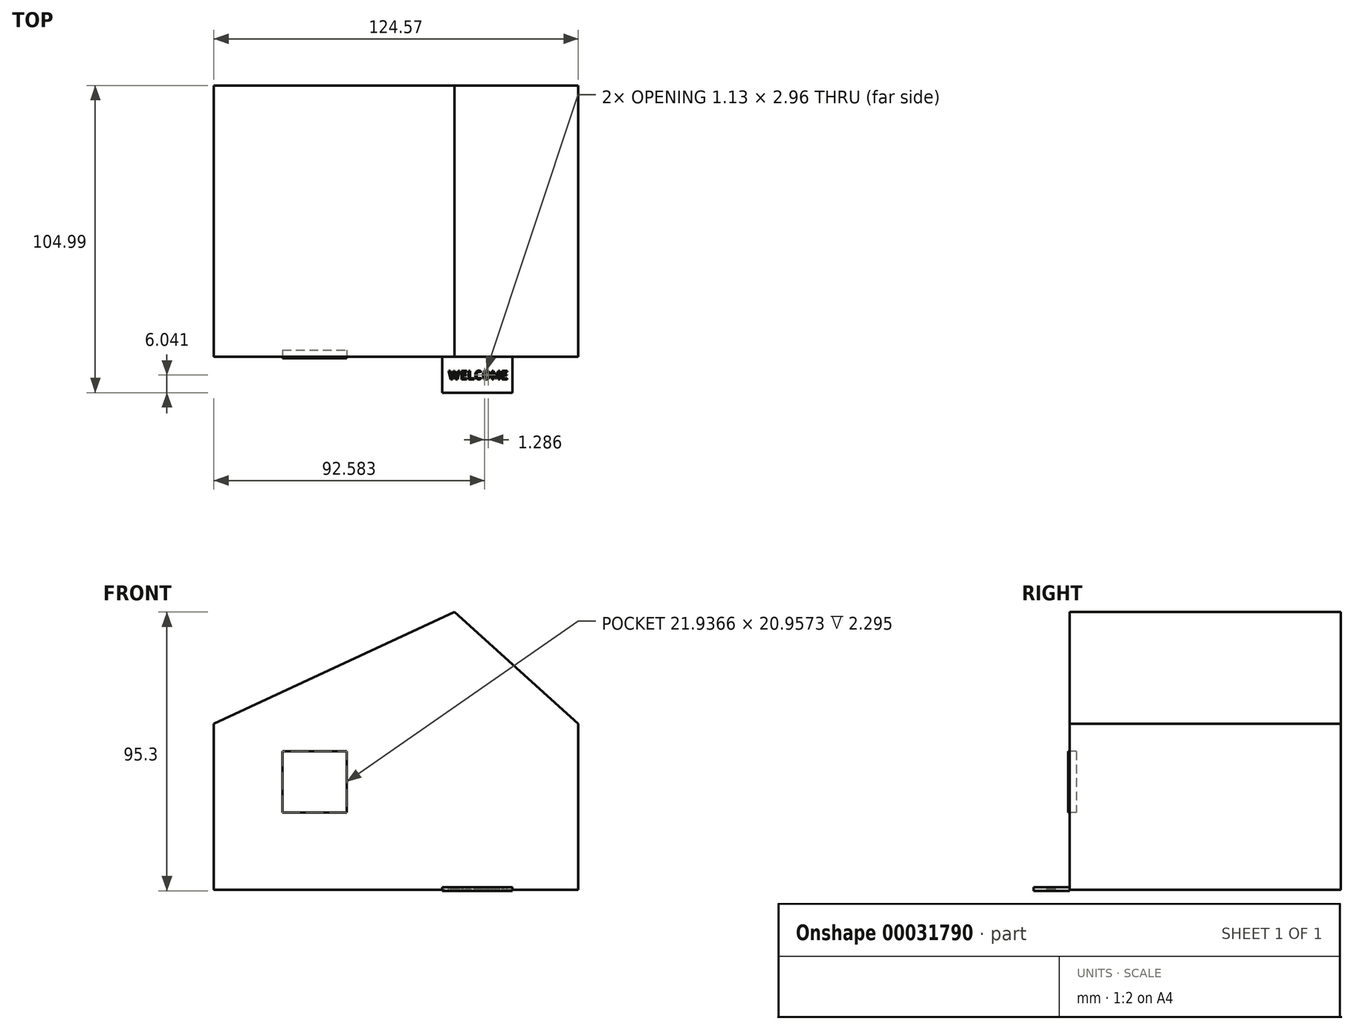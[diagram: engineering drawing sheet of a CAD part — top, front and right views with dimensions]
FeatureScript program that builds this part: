
annotation { "Feature Type Name" : "Feature", "Feature Type Description" : "" }
export const myFeature = defineFeature(function(context is Context, id is Id, definition is map)
    precondition{}
    {
        {
            var Q0;
            Q0=qCreatedBy(makeId("Front.planeOp"),FACE);
            var sketch = newSketch(context, id + "F0", { "sketchPlane" : qUnion([Q0])});
            skLineSegment(sketch, "E0.bottom", {"start": v(-56.21, 22.82) * mm, "end": v(68.36, 22.82) * mm});
            skLineSegment(sketch, "E0.top", {"start": v(-56.21, -33.98) * mm, "end": v(68.36, -33.98) * mm});
            skLineSegment(sketch, "E0.left", {"start": v(-56.21, 22.82) * mm, "end": v(-56.21, -33.98) * mm});
            skLineSegment(sketch, "E0.right", {"start": v(68.36, 22.82) * mm, "end": v(68.36, -33.98) * mm});
            skLineSegment(sketch, "E1", {"start": v(-56.21, 22.82) * mm, "end": v(26.05, 61.01) * mm});
            skLineSegment(sketch, "E2", {"start": v(26.05, 61.01) * mm, "end": v(68.36, 22.82) * mm});
            skSolve(sketch);
        }
        {
            var Q0;
            Q0=makeQuery(id+"F0.imprint","IMPRINT",FACE,{"disambiguationData":[TD([[makeQuery(id+"F0.imprint","IMPRINT",EDGE,{"derivedFrom":sQuery(id+"F0.wireOp",EDGE,"E0.bottom")}),1.0]])]});
            var Q1;
            Q1=makeQuery(id+"F0.imprint","IMPRINT",FACE,{"disambiguationData":[TD([[makeQuery(id+"F0.imprint","IMPRINT",EDGE,{"derivedFrom":sQuery(id+"F0.wireOp",EDGE,"E0.bottom")}),-1.0]])]});
            extrude(context, id + "F1", {"entities" : qUnion([Q0, Q1]), "endBound" : BoundingType.SYMMETRIC, "depth" : 92.66 * mm});
        }
        {
            var Q0;
            Q0=qCreatedBy(makeId("Top.planeOp"),FACE);
            var sketch = newSketch(context, id + "F2", { "sketchPlane" : qUnion([Q0])});
            skLineSegment(sketch, "E3.bottom", {"start": v(21.94, -46.32) * mm, "end": v(45.83, -46.32) * mm});
            skLineSegment(sketch, "E3.top", {"start": v(21.94, -58.66) * mm, "end": v(45.83, -58.66) * mm});
            skLineSegment(sketch, "E3.left", {"start": v(21.94, -46.32) * mm, "end": v(21.94, -58.66) * mm});
            skLineSegment(sketch, "E3.right", {"start": v(45.83, -46.32) * mm, "end": v(45.83, -58.66) * mm});
            skSolve(sketch);
        }
        {
            var Q0;
            Q0 = qSketchRegion(id + "F2", true);
            extrude(context, id + "F3", {"entities" : qUnion([Q0]), "depth" : 1.22 * mm});
        }
        {
            var Q0;
            Q0=makeQuery(id+"F3.opExtrude","SWEPT_BODY",BODY,{"disambiguationData":[OSD([sQuery(id+"F2.wireOp",EDGE,"E3.bottom"),sQuery(id+"F2.wireOp",EDGE,"E3.top"),sQuery(id+"F2.wireOp",EDGE,"E3.left"),sQuery(id+"F2.wireOp",EDGE,"E3.right")])]});
            var Q1;
            Q1=qCreatedBy(makeId("Top.planeOp"),FACE);
            transform(context, id + "F4", {"entities" : qUnion([Q0]), "transformType" : TransformType.TRANSLATION_DISTANCE, "transformDirection" : qUnion([Q1]), "distance" : 34.3 * mm, "oppositeDirection" : true, "makeCopy" : false});
        }
        {
            var Q0;
            Q0=qCreatedBy(makeId("Top.planeOp"),FACE);
            var sketch = newSketch(context, id + "F5", { "sketchPlane" : qUnion([Q0])});
            skText(sketch, "E4", { "text": "WELCOME", "fontName": "AllertaStencil-Regular.ttf"});
            const initialGuessF5  = {"E4": [0.0238, -0.05408, 1, 0, 0.0029]};
            skSetInitialGuess(sketch, initialGuessF5);
            skSolve(sketch);
        }
        {
            var Q0;
            Q0 = qSketchRegion(id + "F5", true);
            extrude(context, id + "F6", {"entities" : qUnion([Q0]), "operationType" : NewBodyOperationType.REMOVE, "oppositeDirection" : true, "depth" : 34.43 * mm});
        }
        {
            var Q0;
            Q0=makeQuery(id+"F1.opExtrude","CAP_FACE",FACE,{"disambiguationData":[OSD([sQuery(id+"F0.wireOp",EDGE,"E0.top"),sQuery(id+"F0.wireOp",EDGE,"E0.left"),sQuery(id+"F0.wireOp",EDGE,"E0.right"),sQuery(id+"F0.wireOp",EDGE,"E1"),sQuery(id+"F0.wireOp",EDGE,"E2")])],"isStart":false});
            var sketch = newSketch(context, id + "F7", { "sketchPlane" : qUnion([Q0])});
            skLineSegment(sketch, "E5.bottom", {"start": v(18.41, 4.4) * mm, "end": v(48.97, 4.4) * mm});
            skLineSegment(sketch, "E5.top", {"start": v(18.41, -33.98) * mm, "end": v(48.97, -33.98) * mm});
            skLineSegment(sketch, "E5.left", {"start": v(18.41, 4.4) * mm, "end": v(18.41, -33.98) * mm});
            skLineSegment(sketch, "E5.right", {"start": v(48.97, 4.4) * mm, "end": v(48.97, -33.98) * mm});
            skSolve(sketch);
        }
        {
            var Q0;
            Q0=makeQuery(id+"F7.imprint","IMPRINT",FACE,{"disambiguationData":[TD([[makeQuery(id+"F7.imprint","IMPRINT",EDGE,{"derivedFrom":sQuery(id+"F7.wireOp",EDGE,"E5.bottom")}),-1.0]])]});
            extrude(context, id + "F8", {"entities" : qUnion([Q0]), "operationType" : NewBodyOperationType.REMOVE, "oppositeDirection" : true, "depth" : 1.56 * mm});
        }
        {
            var Q0;
            Q0=makeQuery(id+"F1.opExtrude","CAP_FACE",FACE,{"disambiguationData":[OSD([sQuery(id+"F0.wireOp",EDGE,"E0.top"),sQuery(id+"F0.wireOp",EDGE,"E0.left"),sQuery(id+"F0.wireOp",EDGE,"E0.right"),sQuery(id+"F0.wireOp",EDGE,"E1"),sQuery(id+"F0.wireOp",EDGE,"E2")])],"isStart":false});
            var sketch = newSketch(context, id + "F9", { "sketchPlane" : qUnion([Q0])});
            skLineSegment(sketch, "E6.bottom", {"start": v(18.41, 4.4) * mm, "end": v(48.97, 4.4) * mm});
            skLineSegment(sketch, "E6.top", {"start": v(18.41, -33.98) * mm, "end": v(48.97, -33.98) * mm});
            skLineSegment(sketch, "E6.left", {"start": v(18.41, 4.4) * mm, "end": v(18.41, -33.98) * mm});
            skLineSegment(sketch, "E6.right", {"start": v(48.97, 4.4) * mm, "end": v(48.97, -33.98) * mm});
            skSolve(sketch);
        }
        {
            var Q0;
            Q0=makeQuery(id+"F9.imprint","IMPRINT",FACE,{"disambiguationData":[TD([[makeQuery(id+"F9.imprint","IMPRINT",EDGE,{"derivedFrom":sQuery(id+"F9.wireOp",EDGE,"E6.bottom")}),-1.0]])]});
            extrude(context, id + "F10", {"entities" : qUnion([Q0]), "operationType" : NewBodyOperationType.ADD, "oppositeDirection" : true, "depth" : 2.07 * mm});
        }
        {
            var Q0;
            Q0=makeQuery(id+"F1.opExtrude","CAP_FACE",FACE,{"disambiguationData":[OSD([sQuery(id+"F0.wireOp",EDGE,"E0.top"),sQuery(id+"F0.wireOp",EDGE,"E0.left"),sQuery(id+"F0.wireOp",EDGE,"E0.right"),sQuery(id+"F0.wireOp",EDGE,"E1"),sQuery(id+"F0.wireOp",EDGE,"E2")])],"isStart":false});
            var sketch = newSketch(context, id + "F11", { "sketchPlane" : qUnion([Q0])});
            skLineSegment(sketch, "E7.bottom", {"start": v(-32.7, 13.42) * mm, "end": v(-10.77, 13.42) * mm});
            skLineSegment(sketch, "E7.top", {"start": v(-32.7, -7.54) * mm, "end": v(-10.77, -7.54) * mm});
            skLineSegment(sketch, "E7.left", {"start": v(-32.7, 13.42) * mm, "end": v(-32.7, -7.54) * mm});
            skLineSegment(sketch, "E7.right", {"start": v(-10.77, 13.42) * mm, "end": v(-10.77, -7.54) * mm});
            skSolve(sketch);
        }
        {
            var Q0;
            Q0=makeQuery(id+"F11.imprint","IMPRINT",FACE,{"disambiguationData":[TD([[makeQuery(id+"F11.imprint","IMPRINT",EDGE,{"derivedFrom":sQuery(id+"F11.wireOp",EDGE,"E7.bottom")}),-1.0]])]});
            extrude(context, id + "F12", {"entities" : qUnion([Q0]), "operationType" : NewBodyOperationType.REMOVE, "oppositeDirection" : true, "depth" : 2.3 * mm});
        }
        {
            var Q0;
            Q0=makeQuery(id+"F1.opExtrude","CAP_FACE",FACE,{"disambiguationData":[OSD([sQuery(id+"F0.wireOp",EDGE,"E0.top"),sQuery(id+"F0.wireOp",EDGE,"E0.left"),sQuery(id+"F0.wireOp",EDGE,"E0.right"),sQuery(id+"F0.wireOp",EDGE,"E1"),sQuery(id+"F0.wireOp",EDGE,"E2")])],"isStart":false});
            var sketch = newSketch(context, id + "F13", { "sketchPlane" : qUnion([Q0])});
            skLineSegment(sketch, "E8.bottom", {"start": v(-32.7, 13.42) * mm, "end": v(-10.77, 13.42) * mm});
            skLineSegment(sketch, "E8.top", {"start": v(-32.7, -7.54) * mm, "end": v(-10.77, -7.54) * mm});
            skLineSegment(sketch, "E8.left", {"start": v(-32.7, 13.42) * mm, "end": v(-32.7, -7.54) * mm});
            skLineSegment(sketch, "E8.right", {"start": v(-10.77, 13.42) * mm, "end": v(-10.77, -7.54) * mm});
            skSolve(sketch);
        }
        {
            var Q0;
            Q0=makeQuery(id+"F13.imprint","IMPRINT",FACE,{"disambiguationData":[TD([[makeQuery(id+"F13.imprint","IMPRINT",EDGE,{"derivedFrom":sQuery(id+"F13.wireOp",EDGE,"E8.bottom")}),-1.0]])]});
            extrude(context, id + "F14", {"entities" : qUnion([Q0]), "operationType" : NewBodyOperationType.ADD, "depth" : 0.53 * mm});
        }
    });
